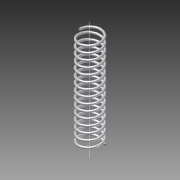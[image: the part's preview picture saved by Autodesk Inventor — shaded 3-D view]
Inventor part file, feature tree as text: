
AUTODESK INVENTOR PART (.ipt)
format: ipt  version: 2012 (Build 160160000, 160)  size: 401,920 bytes
history: native  units: in
note: dims shown in document units (in); Inventor stores cm internally (conversion verified against a paired STEP export)
features: helix x1, sketch x1
ambient origin geometry x8: Origin, YZ Plane, XZ Plane, XY Plane, X Axis, Y Axis, Z Axis, Center Point
bodies: Solid1 (feature_tree)
feature tree (2):
  helix  "Coil1"  [1 undecoded]
  sketch  "Sketch1"  dims[d1=0.02in d2=0.06in d3=0.9in d4=0.3937in d5=0.0in d6=90.0deg d7=90.0deg d8=0.0in d9=0.0in]
note: 1 required parameter value undecoded (feature->parameter linkage not recoverable at this tier; creation-order binding heuristic only, values carry confidence <= 0.55)
